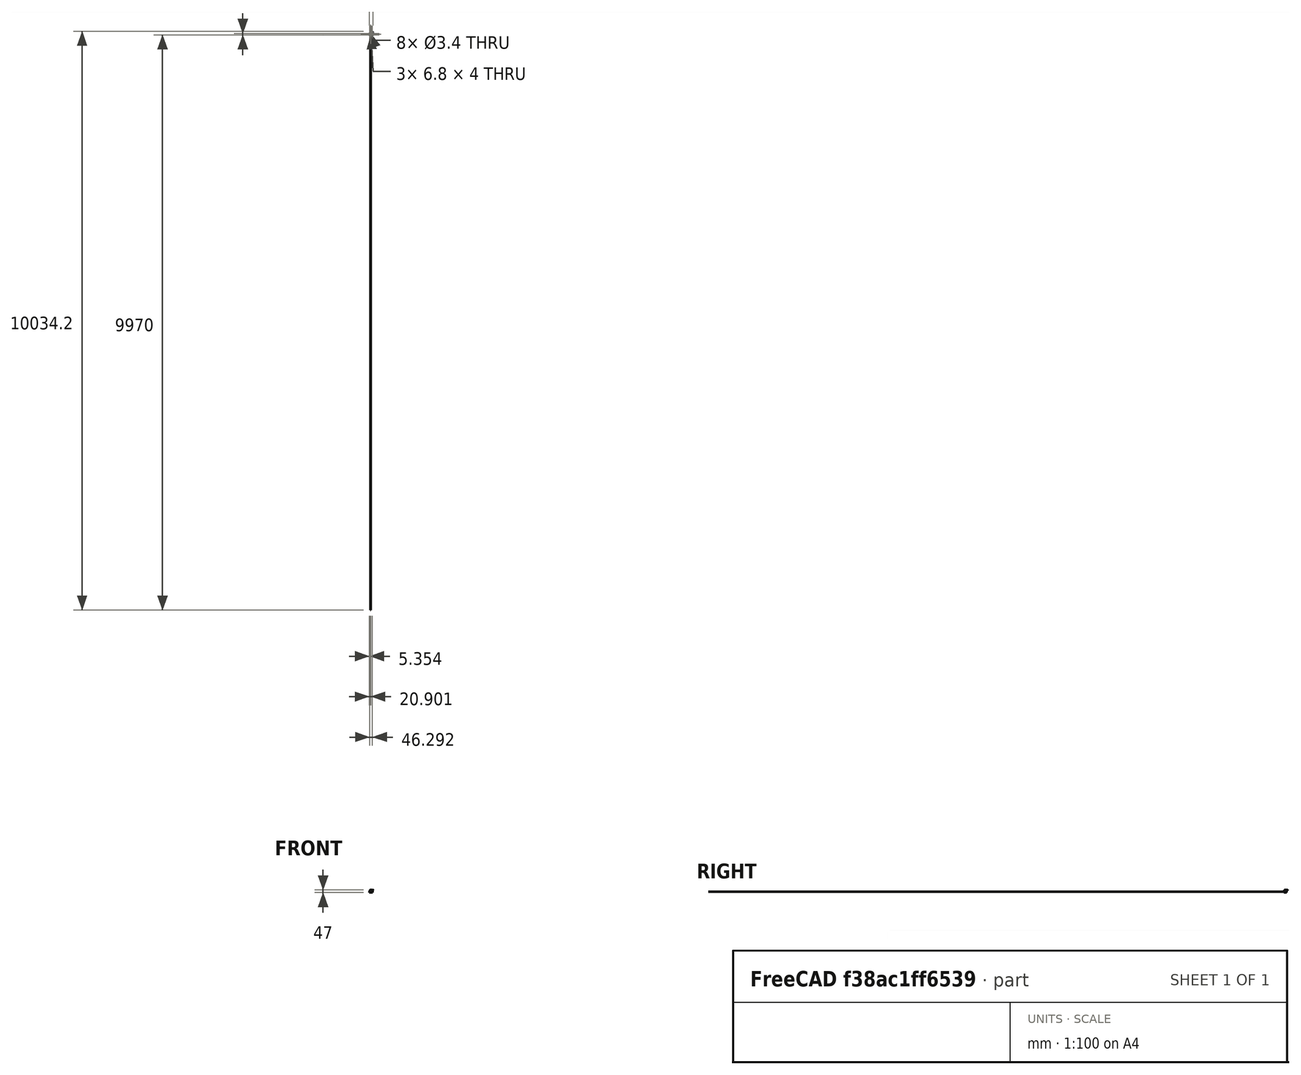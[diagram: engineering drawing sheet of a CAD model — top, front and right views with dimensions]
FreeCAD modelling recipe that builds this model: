
FCSTD DOCUMENT  (FreeCAD 0.14R2935 (Git))
Label: cabeza
License: CC-BY 3.0
LicenseURL: http://creativecommons.org/licenses/by/3.0/
objects: Sketcher::SketchObject×20, PartDesign::Pocket×14, PartDesign::Chamfer×8, PartDesign::Pad×7, PartDesign::Fillet×6, App::DocumentObjectGroup×5, Part::Box×4, Part::FeaturePython×3, Part::Feature×2, Part::Cylinder×1, Mesh::Feature×1, Part::Cut×1
note: 87 computed .brp shape members not serialized (recipe doc carries the construction recipe); baked Part::Feature solids carry a one-line shape summary decoded from their .brp

FEATURE [Part::Box] Box
  Height = 2
  Length = 10
  Width = 12
FEATURE [Sketcher::SketchObject] Sketch
  Placement = pos=(0,0,2) rot=(0,0,1;0rad)
  Support = -> Box [Face6]
  sketch-geometry (1):
    g0: Circle CenterX=4.90431 CenterY=7.27272 CenterZ=0 NormalX=0 NormalY=0 NormalZ=1 Radius=4.25
  constraints (1):
    c: Radius(g0) = 4.25
FEATURE [PartDesign::Pad] Pad
  Length = 2
  Length2 = 100
  Sketch = -> Sketch
  Type = 0
FEATURE [Sketcher::SketchObject] Sketch001
  ExternalGeometry = -> [Pad]
  Placement = pos=(0,0,4) rot=(0,0,1;0rad)
  Support = -> Pad [Face8]
  sketch-geometry (1):
    g0: Circle CenterX=4.90431 CenterY=7.27272 CenterZ=0 NormalX=0 NormalY=0 NormalZ=1 Radius=2
  constraints (2):
    c: Coincident(g0,g-3)
    c: Radius(g0) = 2
FEATURE [PartDesign::Pocket] Pocket  label="camara"
  Length = 1
  Sketch = -> Sketch001
  Type = 0
FEATURE [App::DocumentObjectGroup] Grupo  label="Camera"
  Group = -> [Box,Pad,Pocket]
FEATURE [Part::FeaturePython] Clone  label="camara001"  # Draft clone (typed FeaturePython)
  Objects = -> [Pocket]
  Placement = pos=(1.5,0,-16) rot=(0,0,1;0rad)
  Scale = (1,1,1)
FEATURE [Part::Cylinder] Cylinder
  Angle = 360
  Height = 2
  Radius = 11.5
FEATURE [Sketcher::SketchObject] Sketch002
  Placement = pos=(0,0,2) rot=(0,0,1;0rad)
  Support = -> Cylinder [Face2]
  sketch-geometry (6):
    g0: LineSegment StartX=-3 StartY=3 StartZ=0 EndX=3 EndY=3 EndZ=0
    g1: LineSegment StartX=3 StartY=3 StartZ=0 EndX=3 EndY=-3 EndZ=0
    g2: LineSegment StartX=3 StartY=-3 StartZ=0 EndX=-3 EndY=-3 EndZ=0
    g3: LineSegment StartX=-3 StartY=-3 StartZ=0 EndX=-3 EndY=3 EndZ=0
    g4: LineSegment [constr] StartX=-3 StartY=3 StartZ=0 EndX=3 EndY=-3 EndZ=0
    g5: LineSegment [constr] StartX=3 StartY=3 StartZ=0 EndX=-3 EndY=-3 EndZ=0
  constraints (16):
    c: Coincident(g0,g1)
    c: Coincident(g1,g2)
    c: Coincident(g2,g3)
    c: Coincident(g3,g0)
    c: Horizontal(g0)
    c: Horizontal(g2)
    c: Vertical(g1)
    c: Vertical(g3)
    c: Equal(g0,g1)
    c: DistanceX(g2) = -6
    c: Coincident(g5,g0)
    c: Coincident(g5,g2)
    c: Coincident(g4,g1)
    c: Coincident(g4,g0)
    c: PointOnObject(g-1,g5)
    c: PointOnObject(g-1,g4)
FEATURE [PartDesign::Pad] Pad001
  Length = 1
  Length2 = 100
  Sketch = -> Sketch002
  Type = 0
FEATURE [Sketcher::SketchObject] Sketch003
  Placement = pos=(0,0,3) rot=(0,0,1;0rad)
  Support = -> Pad001 [Face8]
  sketch-geometry (1):
    g0: Circle CenterX=0 CenterY=0 CenterZ=0 NormalX=0 NormalY=0 NormalZ=1 Radius=2
  constraints (2):
    c: Coincident(g0,g-1)
    c: Radius(g0) = 2
FEATURE [PartDesign::Pocket] Pocket001
  Length = 1
  Sketch = -> Sketch003
  Type = 0
FEATURE [Sketcher::SketchObject] Sketch004
  ExternalGeometry = -> [Pocket001]
  Placement = pos=(0,0,2) rot=(0,0,1;0rad)
  Support = -> Pocket001 [Face2]
  sketch-geometry (28):
    g0: LineSegment StartX=-3 StartY=9.7 StartZ=0 EndX=3 EndY=9.7 EndZ=0
    g1: LineSegment StartX=3 StartY=9.7 StartZ=0 EndX=3 EndY=3.7 EndZ=0
    g2: LineSegment StartX=3 StartY=3.7 StartZ=0 EndX=-3 EndY=3.7 EndZ=0
    g3: LineSegment StartX=-3 StartY=3.7 StartZ=0 EndX=-3 EndY=9.7 EndZ=0
    g4: LineSegment StartX=-9.7 StartY=3 StartZ=0 EndX=-3.7 EndY=3 EndZ=0
    g5: LineSegment StartX=-3.7 StartY=3 StartZ=0 EndX=-3.7 EndY=-3 EndZ=0
    g6: LineSegment StartX=-3.7 StartY=-3 StartZ=0 EndX=-9.7 EndY=-3 EndZ=0
    g7: LineSegment StartX=-9.7 StartY=-3 StartZ=0 EndX=-9.7 EndY=3 EndZ=0
    g8: LineSegment StartX=-3 StartY=-3.7 StartZ=0 EndX=3 EndY=-3.7 EndZ=0
    g9: LineSegment StartX=3 StartY=-3.7 StartZ=0 EndX=3 EndY=-9.7 EndZ=0
    g10: LineSegment StartX=3 StartY=-9.7 StartZ=0 EndX=-3 EndY=-9.7 EndZ=0
    g11: LineSegment StartX=-3 StartY=-9.7 StartZ=0 EndX=-3 EndY=-3.7 EndZ=0
    g12: LineSegment StartX=3.7 StartY=3 StartZ=0 EndX=9.7 EndY=3 EndZ=0
    g13: LineSegment StartX=9.7 StartY=3 StartZ=0 EndX=9.7 EndY=-3 EndZ=0
    g14: LineSegment StartX=9.7 StartY=-3 StartZ=0 EndX=3.7 EndY=-3 EndZ=0
    g15: LineSegment StartX=3.7 StartY=-3 StartZ=0 EndX=3.7 EndY=3 EndZ=0
    g16: LineSegment [constr] StartX=-3 StartY=9.7 StartZ=0 EndX=3 EndY=3.7 EndZ=0
    g17: LineSegment [constr] StartX=3 StartY=9.7 StartZ=0 EndX=-3 EndY=3.7 EndZ=0
    g18: LineSegment [constr] StartX=3.7 StartY=3 StartZ=0 EndX=9.7 EndY=-3 EndZ=0
    g19: LineSegment [constr] StartX=9.7 StartY=3 StartZ=0 EndX=3.7 EndY=-3 EndZ=0
    g20: LineSegment [constr] StartX=-9.7 StartY=3 StartZ=0 EndX=-3.7 EndY=-3 EndZ=0
    g21: LineSegment [constr] StartX=-3.7 StartY=3 StartZ=0 EndX=-9.7 EndY=-3 EndZ=0
    g22: LineSegment [constr] StartX=-3 StartY=-3.7 StartZ=0 EndX=3 EndY=-9.7 EndZ=0
    g23: LineSegment [constr] StartX=3 StartY=-3.7 StartZ=0 EndX=-3 EndY=-9.7 EndZ=0
    g24: GeomPoint [constr] X=0 Y=-6.7 Z=0
    g25: GeomPoint [constr] X=6.7 Y=0 Z=0
    g26: GeomPoint [constr] X=-6.7 Y=0 Z=0
    g27: GeomPoint [constr] X=0 Y=6.7 Z=0
  constraints (72):
    c: Coincident(g0,g1)
    c: Coincident(g1,g2)
    c: Coincident(g2,g3)
    c: Coincident(g3,g0)
    c: Horizontal(g0)
    c: Horizontal(g2)
    c: Vertical(g1)
    c: Vertical(g3)
    c: Equal(g3,g2)
    c: Equal(g2,g-3)
    c: Coincident(g4,g5)
    c: Coincident(g5,g6)
    c: Coincident(g6,g7)
    c: Coincident(g7,g4)
    c: Horizontal(g4)
    c: Horizontal(g6)
    c: Vertical(g5)
    c: Vertical(g7)
    c: Coincident(g8,g9)
    c: Coincident(g9,g10)
    c: Coincident(g10,g11)
    c: Coincident(g11,g8)
    c: Horizontal(g8)
    c: Horizontal(g10)
    c: Vertical(g9)
    c: Vertical(g11)
    c: Coincident(g12,g13)
    c: Coincident(g13,g14)
    c: Coincident(g14,g15)
    c: Coincident(g15,g12)
    c: Horizontal(g12)
    c: Horizontal(g14)
    c: Vertical(g13)
    c: Vertical(g15)
    c: Equal(g12,g15)
    c: Equal(g15,g8)
    c: Equal(g8,g9)
    c: Equal(g9,g6)
    c: Equal(g6,g5)
    c: Equal(g2,g12)
    c: Coincident(g23,g10)
    c: Coincident(g22,g8)
    c: Coincident(g23,g8)
    c: Coincident(g22,g9)
    c: PointOnObject(g24,g-2)
    c: PointOnObject(g24,g23)
    c: PointOnObject(g24,g22)
    c: Coincident(g19,g12)
    c: Coincident(g18,g13)
    c: Coincident(g18,g12)
    c: Coincident(g19,g14)
    c: Coincident(g16,g1)
    c: Coincident(g17,g0)
    c: Coincident(g17,g2)
    c: Coincident(g16,g0)
    c: Coincident(g21,g4)
    c: Coincident(g20,g4)
    c: Coincident(g21,g6)
    c: Coincident(g20,g5)
    c: PointOnObject(g25,g-1)
    c: PointOnObject(g26,g-1)
    c: PointOnObject(g27,g-2)
    c: PointOnObject(g26,g20)
    c: PointOnObject(g26,g21)
    c: PointOnObject(g25,g19)
    c: PointOnObject(g25,g18)
    c: PointOnObject(g27,g16)
    c: PointOnObject(g27,g17)
    c: Distance(g-4,g4) = 0.7
    c: Distance(g-4,g8) = 0.7
    c: Distance(g-5,g14) = 0.7
    c: Distance(g2,g-4) = 0.7
FEATURE [PartDesign::Pad] Pad002
  Length = 1
  Length2 = 100
  Sketch = -> Sketch004
  Type = 0
FEATURE [Sketcher::SketchObject] Sketch005
  ExternalGeometry = -> [Pad002]
  Placement = pos=(0,0,3) rot=(0,0,1;0rad)
  Support = -> Pad002 [Face26]
  sketch-geometry (4):
    g0: Circle CenterX=0 CenterY=6.61559 CenterZ=0 NormalX=0 NormalY=0 NormalZ=1 Radius=2
    g1: Circle CenterX=-6.61558 CenterY=0 CenterZ=0 NormalX=0 NormalY=0 NormalZ=1 Radius=2
    g2: Circle CenterX=6.71215 CenterY=0 CenterZ=0 NormalX=0 NormalY=0 NormalZ=1 Radius=2
    g3: Circle CenterX=0 CenterY=-6.71214 CenterZ=0 NormalX=0 NormalY=0 NormalZ=1 Radius=2
  constraints (8):
    c: Equal(g1,g0)
    c: Equal(g0,g-3)
    c: Equal(g-3,g2)
    c: Equal(g2,g3)
    c: PointOnObject(g2,g-1)
    c: PointOnObject(g0,g-2)
    c: PointOnObject(g1,g-1)
    c: PointOnObject(g3,g-2)
FEATURE [PartDesign::Pocket] Pocket002
  Length = 1
  Sketch = -> Sketch005
  Type = 0
FEATURE [Part::FeaturePython] Clone001  label="ojo001"  # Draft clone (typed FeaturePython)
  Objects = -> [Pocket002]
  Placement = pos=(-7,-6,-13) rot=(0,0,1;0rad)
  Scale = (1,1,1)
FEATURE [App::DocumentObjectGroup] Grupo001  label="ojo"
  Group = -> [Cylinder,Pad001,Pocket001,Pad002,Pocket002]
FEATURE [Part::FeaturePython] Clone002  label="ojo002"  # Draft clone (typed FeaturePython)
  Objects = -> [Pocket002]
  Placement = pos=(21,-7,-13) rot=(0,0,1;0rad)
  Scale = (1,1,1)
FEATURE [Part::Box] Box001
  Height = 4
  Length = 35
  Placement = pos=(-11,-31,-17) rot=(0,0,1;0rad)
  Width = 47
FEATURE [Mesh::Feature] _g_servo  label="9g_servo"
  Placement = pos=(0,-7,-24) rot=(0.57735,0.57735,0.57735;2.0944rad)
FEATURE [Sketcher::SketchObject] Sketch006
  ExternalGeometry = -> [Box001]
  Placement = pos=(-11,-31,-17) rot=(1,0,0;3.14159rad)
  Support = -> Box001 [Face5]
  sketch-geometry (9):
    g0: LineSegment StartX=6.5 StartY=-7.91944 StartZ=0 EndX=13.302 EndY=-7.91944 EndZ=0
    g1: LineSegment StartX=13.302 StartY=-7.91944 StartZ=0 EndX=13.302 EndY=-11.9194 EndZ=0
    g2: LineSegment StartX=13.302 StartY=-11.9194 StartZ=0 EndX=6.5 EndY=-11.9194 EndZ=0
    g3: LineSegment StartX=6.5 StartY=-11.9194 StartZ=0 EndX=6.5 EndY=-7.91944 EndZ=0
    g4: LineSegment StartX=6.5 StartY=-35.9194 StartZ=0 EndX=13.302 EndY=-35.9194 EndZ=0
    g5: LineSegment StartX=13.302 StartY=-35.9194 StartZ=0 EndX=13.302 EndY=-39.9194 EndZ=0
    g6: LineSegment StartX=13.302 StartY=-39.9194 StartZ=0 EndX=6.5 EndY=-39.9194 EndZ=0
    g7: LineSegment StartX=6.5 StartY=-39.9194 StartZ=0 EndX=6.5 EndY=-35.9194 EndZ=0
    g8: LineSegment [constr] StartX=6.5 StartY=0 StartZ=0 EndX=6.5 EndY=-47 EndZ=0
  constraints (27):
    c: Coincident(g0,g1)
    c: Coincident(g1,g2)
    c: Coincident(g2,g3)
    c: Coincident(g3,g0)
    c: Horizontal(g0)
    c: Horizontal(g2)
    c: Vertical(g1)
    c: Vertical(g3)
    c: Coincident(g4,g5)
    c: Coincident(g5,g6)
    c: Coincident(g6,g7)
    c: Coincident(g7,g4)
    c: Horizontal(g4)
    c: Horizontal(g6)
    c: Vertical(g5)
    c: Vertical(g7)
    c: Equal(g2,g4)
    c: Vertical(g8)
    c: PointOnObject(g8,g-3)
    c: PointOnObject(g8,g-1)
    c: PointOnObject(g0,g8)
    c: PointOnObject(g4,g8)
    c: Equal(g1,g5)
    c: DistanceY(g1) = -4
    c: Distance(g2,g4) = 24
    c: Distance(g6,g8) = 7.08056
    c: Distance(g-3,g8) = 6.5
FEATURE [PartDesign::Pad] Pad003
  Length = 14
  Length2 = 100
  Placement = pos=(-11,-31,-17) rot=(0,0,1;0rad)
  Sketch = -> Sketch006
  Type = 0
FEATURE [Sketcher::SketchObject] Sketch007
  ExternalGeometry = -> [Pad003]
  Placement = pos=(2.30204,-31,-17) rot=(0.57735,0.57735,0.57735;2.0944rad)
  Support = -> Pad003 [Face7]
  sketch-geometry (3):
    g0: Circle CenterX=9.93523 CenterY=-7.03791 CenterZ=0 NormalX=0 NormalY=0 NormalZ=1 Radius=1.64716
    g1: Circle CenterX=37.8885 CenterY=-7.03791 CenterZ=0 NormalX=0 NormalY=0 NormalZ=1 Radius=1.53113
    g2: LineSegment [constr] StartX=35.9194 StartY=-7.03791 StartZ=0 EndX=11.9194 EndY=-7.03791 EndZ=0
  constraints (5):
    c: PointOnObject(g2,g-3)
    c: Horizontal(g2)
    c: PointOnObject(g2,g-4)
    c: PointOnObject(g0,g2)
    c: PointOnObject(g1,g2)
FEATURE [PartDesign::Pocket] Pocket003
  Length = 7
  Placement = pos=(-11,-31,-17) rot=(0,0,1;0rad)
  Sketch = -> Sketch007
  Type = 0
FEATURE [Sketcher::SketchObject] Sketch008
  ExternalGeometry = -> [Pocket003]
  Placement = pos=(-11,-31,-17) rot=(1,0,0;3.14159rad)
  Support = -> Pocket003 [Face5]
  sketch-geometry (6):
    g0: ArcOfCircle CenterX=31.6459 CenterY=-23.9498 CenterZ=0 NormalX=0 NormalY=0 NormalZ=1 Radius=11.5 StartAngle=5.00835 EndAngle=7.55802
    g1: LineSegment [constr] StartX=35 StartY=-12.9498 StartZ=0 EndX=0 EndY=-12.9498 EndZ=0
    g2: LineSegment [constr] StartX=35 StartY=-34.9498 StartZ=0 EndX=0 EndY=-34.9498 EndZ=0
    g3: ArcOfCircle CenterX=3.3541 CenterY=-23.9498 CenterZ=0 NormalX=0 NormalY=0 NormalZ=1 Radius=11.5 StartAngle=1.86676 EndAngle=4.41643
    g4: LineSegment StartX=35 StartY=-12.9498 StartZ=0 EndX=35 EndY=-34.9498 EndZ=0
    g5: LineSegment StartX=0 StartY=-12.9498 StartZ=0 EndX=0 EndY=-34.9498 EndZ=0
  constraints (20):
    c: PointOnObject(g0,g-3)
    c: PointOnObject(g0,g-3)
    c: Distance(g0,g0) = 22
    c: Radius(g0) = 11.5
    c: Horizontal(g1)
    c: Horizontal(g2)
    c: Distance(g-3,g0) = 12.9498
    c: Coincident(g1,g0)
    c: PointOnObject(g1,g-2)
    c: Coincident(g2,g0)
    c: PointOnObject(g2,g-2)
    c: Coincident(g3,g2)
    c: Coincident(g3,g1)
    c: Equal(g0,g3)
    c: Vertical(g4)
    c: Coincident(g4,g0)
    c: Coincident(g4,g0)
    c: Vertical(g5)
    c: Coincident(g5,g1)
    c: Coincident(g5,g2)
FEATURE [PartDesign::Pad] Pad004
  Length = 4
  Length2 = 100
  Placement = pos=(-11,-31,-17) rot=(0,0,1;0rad)
  Reversed = true
  Sketch = -> Sketch008
  Type = 0
FEATURE [Sketcher::SketchObject] Sketch009
  ExternalGeometry = -> [Pad004]
  Placement = pos=(-11,-31,-13) rot=(0,0,1;0rad)
  Support = -> Pad004 [Face4]
  sketch-geometry (6):
    g0: Circle CenterX=17.5 CenterY=38.5843 CenterZ=0 NormalX=0 NormalY=0 NormalZ=1 Radius=4.5
    g1: LineSegment [constr] StartX=0 StartY=38.5843 StartZ=0 EndX=17.5 EndY=38.5843 EndZ=0
    g2: LineSegment [constr] StartX=17.5 StartY=38.5843 StartZ=0 EndX=35 EndY=38.5843 EndZ=0
    g3: Circle CenterX=-5.6459 CenterY=23.9498 CenterZ=0 NormalX=0 NormalY=0 NormalZ=1 Radius=1.7
    g4: Circle CenterX=40.6459 CenterY=23.9498 CenterZ=0 NormalX=0 NormalY=0 NormalZ=1 Radius=1.7
    g5: LineSegment [constr] StartX=-8.1459 StartY=23.9498 StartZ=0 EndX=43.1459 EndY=23.9498 EndZ=0
  constraints (19):
    c: Horizontal(g1)
    c: Horizontal(g2)
    c: PointOnObject(g1,g-2)
    c: PointOnObject(g2,g-3)
    c: Coincident(g2,g0)
    c: Coincident(g1,g0)
    c: Equal(g1,g2)
    c: Radius(g0) = 4.5
    c: DistanceY(g-1,g2) = 38.5843
    c: Horizontal(g5)
    c: PointOnObject(g5,g-5)
    c: PointOnObject(g5,g-4)
    c: PointOnObject(g3,g5)
    c: PointOnObject(g4,g5)
    c: Radius(g4) = 1.7
    c: Radius(g3) = 1.7
    c: Distance(g3,g5) = 2.5
    c: Distance(g4,g5) = 2.5
    c: PointOnObject(g-5,g5)
FEATURE [PartDesign::Pocket] Pocket004
  Length = 4
  Placement = pos=(-11,-31,-17) rot=(0,0,1;0rad)
  Sketch = -> Sketch009
  Type = 0
FEATURE [Part::Feature] Pocket004001  label="Pocket005"
  shape: bbox 51.29 x 47 x 18 mm, 26 faces (baked)
FEATURE [PartDesign::Chamfer] Chamfer
  Base = -> Pocket004001 [Edge6]
  Size = 10
FEATURE [PartDesign::Chamfer] Chamfer001
  Base = -> Chamfer [Edge3]
  Size = 10
FEATURE [PartDesign::Fillet] Fillet
  Base = -> Chamfer001 [Edge3]
  Radius = 10
FEATURE [PartDesign::Fillet] Fillet001
  Base = -> Fillet [Edge3]
  Radius = 10
FEATURE [PartDesign::Fillet] Fillet002
  Base = -> Fillet001 [Edge45]
  Radius = 3
FEATURE [PartDesign::Fillet] Fillet003
  Base = -> Fillet002 [Edge43]
  Radius = 3
FEATURE [PartDesign::Chamfer] Chamfer002
  Base = -> Fillet003 [Edge46]
  Size = 10
FEATURE [PartDesign::Chamfer] Chamfer003
  Base = -> Chamfer002 [Edge29]
  Size = 10
FEATURE [Sketcher::SketchObject] Sketch010
  ExternalGeometry = -> [Chamfer003]
  Placement = pos=(0,0,-13) rot=(0,0,1;0rad)
  Support = -> Chamfer003 [Face29]
  sketch-geometry (9):
    g0: LineSegment [constr] StartX=-16.6459 StartY=-7.0502 StartZ=0 EndX=29.6459 EndY=-7.0502 EndZ=0
    g1: Circle CenterX=3.3541 CenterY=-7.0502 CenterZ=0 NormalX=0 NormalY=0 NormalZ=1 Radius=1.7
    g2: Circle CenterX=9.6459 CenterY=-7.0502 CenterZ=0 NormalX=0 NormalY=0 NormalZ=1 Radius=1.7
    g3: LineSegment [constr] StartX=-1 StartY=-7.0502 StartZ=0 EndX=-1 EndY=-31 EndZ=0
    g4: LineSegment [constr] StartX=14 StartY=-7.0502 StartZ=0 EndX=14 EndY=-31 EndZ=0
    g5: LineSegment StartX=-1 StartY=-23.5 StartZ=0 EndX=14 EndY=-23.5 EndZ=0
    g6: LineSegment StartX=14 StartY=-23.5 StartZ=0 EndX=14 EndY=-26.5 EndZ=0
    g7: LineSegment StartX=14 StartY=-26.5 StartZ=0 EndX=-1 EndY=-26.5 EndZ=0
    g8: LineSegment StartX=-1 StartY=-26.5 StartZ=0 EndX=-1 EndY=-23.5 EndZ=0
  constraints (27):
    c: Horizontal(g0)
    c: Coincident(g0,g-4)
    c: Coincident(g0,g-3)
    c: PointOnObject(g1,g0)
    c: PointOnObject(g2,g0)
    c: Radius(g2) = 1.7
    c: Radius(g1) = 1.7
    c: Distance(g0,g1) = 20
    c: Distance(g2,g0) = 20
    c: Vertical(g3)
    c: Coincident(g3,g-5)
    c: PointOnObject(g3,g0)
    c: Vertical(g4)
    c: Coincident(g4,g-5)
    c: PointOnObject(g4,g0)
    c: Coincident(g5,g6)
    c: Coincident(g6,g7)
    c: Coincident(g7,g8)
    c: Coincident(g8,g5)
    c: Horizontal(g5)
    c: Horizontal(g7)
    c: Vertical(g6)
    c: Vertical(g8)
    c: DistanceY(g6) = -3
    c: PointOnObject(g7,g3)
    c: PointOnObject(g6,g4)
    c: Distance(g7,g3) = 4.5
FEATURE [PartDesign::Pocket] Pocket004002
  Length = 5
  Sketch = -> Sketch010
  Type = 0
FEATURE [Sketcher::SketchObject] Sketch011
  Placement = pos=(0,8.91944,0) rot=(0,0.707107,0.707107;3.14159rad)
  Support = -> Pocket004002 [Face18]
  sketch-geometry (4):
    g0: LineSegment StartX=-1.74892 StartY=-26.7435 StartZ=0 EndX=3.95108 EndY=-26.7435 EndZ=0
    g1: LineSegment StartX=3.95108 StartY=-26.7435 StartZ=0 EndX=3.95108 EndY=-29.3435 EndZ=0
    g2: LineSegment StartX=3.95108 StartY=-29.3435 StartZ=0 EndX=-1.74892 EndY=-29.3435 EndZ=0
    g3: LineSegment StartX=-1.74892 StartY=-29.3435 StartZ=0 EndX=-1.74892 EndY=-26.7435 EndZ=0
  constraints (10):
    c: Coincident(g0,g1)
    c: Coincident(g1,g2)
    c: Coincident(g2,g3)
    c: Coincident(g3,g0)
    c: Horizontal(g0)
    c: Horizontal(g2)
    c: Vertical(g1)
    c: Vertical(g3)
    c: DistanceY(g1) = -2.6
    c: DistanceX(g2) = -5.7
FEATURE [PartDesign::Pocket] Pocket004003
  Length = 5
  Sketch = -> Sketch011
  Type = 1
FEATURE [Sketcher::SketchObject] Sketch012
  ExternalGeometry = -> [Pocket004003]
  Placement = pos=(0,0,-31) rot=(1,0,0;3.14159rad)
  Support = -> Pocket004003 [Face37]
  sketch-geometry (6):
    g0: LineSegment [constr] StartX=-4.5 StartY=23.0806 StartZ=0 EndX=2.30204 EndY=19.0806 EndZ=0
    g1: LineSegment [constr] StartX=2.30204 StartY=23.0806 StartZ=0 EndX=-4.5 EndY=19.0806 EndZ=0
    g2: Circle CenterX=-1.09898 CenterY=21.0806 CenterZ=0 NormalX=0 NormalY=0 NormalZ=1 Radius=1.7
    g3: LineSegment [constr] StartX=-4.5 StartY=-4.91944 StartZ=0 EndX=2.30204 EndY=-8.91944 EndZ=0
    g4: LineSegment [constr] StartX=2.30204 StartY=-4.91944 StartZ=0 EndX=-4.5 EndY=-8.91944 EndZ=0
    g5: Circle CenterX=-1.09898 CenterY=-6.91944 CenterZ=0 NormalX=0 NormalY=0 NormalZ=1 Radius=1.7
  constraints (14):
    c: Coincident(g1,g-4)
    c: Coincident(g1,g-3)
    c: Coincident(g0,g-4)
    c: Coincident(g0,g-3)
    c: PointOnObject(g2,g1)
    c: PointOnObject(g2,g0)
    c: Radius(g2) = 1.7
    c: Coincident(g4,g-6)
    c: Coincident(g4,g-5)
    c: Coincident(g3,g-6)
    c: Coincident(g3,g-5)
    c: PointOnObject(g5,g4)
    c: PointOnObject(g5,g3)
    c: Radius(g5) = 1.7
FEATURE [PartDesign::Pocket] Pocket004004
  Length = 4
  Sketch = -> Sketch012
  Type = 0
FEATURE [Part::Box] Box002
  Height = 26
  Length = 36
  Placement = pos=(-12,-31,-43) rot=(0,0,1;0rad)
  Width = 47
FEATURE [PartDesign::Pocket] Pocket004005
  Length = 4
  Sketch = -> Sketch012
  Type = 0
FEATURE [Part::Feature] Pocket004006  label="cara"
  shape: bbox 51.29 x 47 x 18 mm, 50 faces (baked)
FEATURE [PartDesign::Fillet] Fillet004
  Base = -> Box002 [Edge7]
  Placement = pos=(-12,-31,-43) rot=(0,0,1;0rad)
  Radius = 17
FEATURE [PartDesign::Fillet] Fillet005
  Base = -> Fillet004 [Edge15]
  Placement = pos=(-12,-31,-43) rot=(0,0,1;0rad)
  Radius = 17
FEATURE [PartDesign::Chamfer] Chamfer004
  Base = -> Fillet005 [Edge16]
  Placement = pos=(-12,-31,-43) rot=(0,0,1;0rad)
  Size = 10
FEATURE [PartDesign::Chamfer] Chamfer005
  Base = -> Chamfer004 [Edge16]
  Placement = pos=(-12,-31,-43) rot=(0,0,1;0rad)
  Size = 10
FEATURE [Part::Box] Box003
  Height = 26
  Length = 36
  Placement = pos=(-12,-31,-43) rot=(0,0,1;0rad)
  Width = 10
FEATURE [Part::Cut] Cut
  Base = -> Chamfer005
  Tool = -> Box003
FEATURE [Sketcher::SketchObject] Sketch013
  ExternalGeometry = -> [Cut]
  Placement = pos=(0,-21,0) rot=(1,0,0;1.5708rad)
  Support = -> Cut [Face7]
  sketch-geometry (4):
    g0: LineSegment StartX=-9 StartY=-17 StartZ=0 EndX=21 EndY=-17 EndZ=0
    g1: LineSegment StartX=21 StartY=-17 StartZ=0 EndX=21 EndY=-40 EndZ=0
    g2: LineSegment StartX=21 StartY=-40 StartZ=0 EndX=-9 EndY=-40 EndZ=0
    g3: LineSegment StartX=-9 StartY=-40 StartZ=0 EndX=-9 EndY=-17 EndZ=0
  constraints (12):
    c: Coincident(g0,g1)
    c: Coincident(g1,g2)
    c: Coincident(g2,g3)
    c: Coincident(g3,g0)
    c: Horizontal(g0)
    c: Horizontal(g2)
    c: Vertical(g1)
    c: Vertical(g3)
    c: PointOnObject(g0,g-5)
    c: Distance(g-5,g0) = 3
    c: Distance(g-5,g0) = 3
    c: Distance(g2,g-6) = 3
FEATURE [PartDesign::Pocket] Pocket004007
  Length = 27
  Sketch = -> Sketch013
  Type = 0
FEATURE [Sketcher::SketchObject] Sketch014
  ExternalGeometry = -> [Pocket004007]
  Placement = pos=(0,0,-17) rot=(0,0,1;0rad)
  Support = -> Pocket004007 [Face1]
  sketch-geometry (4):
    g0: LineSegment StartX=-0.588067 StartY=13.0845 StartZ=0 EndX=12.9735 EndY=13.0845 EndZ=0
    g1: LineSegment StartX=12.9735 StartY=13.0845 StartZ=0 EndX=12.9735 EndY=6 EndZ=0
    g2: LineSegment StartX=12.9735 StartY=6 StartZ=0 EndX=-0.588067 EndY=6 EndZ=0
    g3: LineSegment StartX=-0.588067 StartY=6 StartZ=0 EndX=-0.588067 EndY=13.0845 EndZ=0
  constraints (9):
    c: Coincident(g0,g1)
    c: Coincident(g1,g2)
    c: Coincident(g2,g3)
    c: Coincident(g3,g0)
    c: Horizontal(g0)
    c: Horizontal(g2)
    c: Vertical(g1)
    c: Vertical(g3)
    c: PointOnObject(g2,g-3)
FEATURE [PartDesign::Pocket] Pocket004008
  Length = 23
  Sketch = -> Sketch014
  Type = 0
FEATURE [Sketcher::SketchObject] Sketch015
  ExternalGeometry = -> [Pocket004008]
  Placement = pos=(0,0,-43) rot=(1,0,0;3.14159rad)
  Support = -> Pocket004008 [Face15]
  sketch-geometry (8):
    g0: LineSegment StartX=-22 StartY=21 StartZ=0 EndX=-12 EndY=21 EndZ=0
    g1: LineSegment StartX=-12 StartY=21 StartZ=0 EndX=-12 EndY=1 EndZ=0
    g2: LineSegment StartX=-12 StartY=1 StartZ=0 EndX=-22 EndY=1 EndZ=0
    g3: LineSegment StartX=-22 StartY=1 StartZ=0 EndX=-22 EndY=21 EndZ=0
    g4: LineSegment StartX=34 StartY=21 StartZ=0 EndX=24 EndY=21 EndZ=0
    g5: LineSegment StartX=24 StartY=21 StartZ=0 EndX=24 EndY=1 EndZ=0
    g6: LineSegment StartX=24 StartY=1 StartZ=0 EndX=34 EndY=1 EndZ=0
    g7: LineSegment StartX=34 StartY=1 StartZ=0 EndX=34 EndY=21 EndZ=0
  constraints (22):
    c: Coincident(g0,g1)
    c: Coincident(g1,g2)
    c: Coincident(g2,g3)
    c: Coincident(g3,g0)
    c: Horizontal(g0)
    c: Horizontal(g2)
    c: Vertical(g1)
    c: Vertical(g3)
    c: Coincident(g-3,g0)
    c: Coincident(g1,g-3)
    c: Coincident(g4,g5)
    c: Coincident(g5,g6)
    c: Coincident(g6,g7)
    c: Coincident(g7,g4)
    c: Horizontal(g4)
    c: Horizontal(g6)
    c: Vertical(g5)
    c: Vertical(g7)
    c: Coincident(g5,g-4)
    c: Coincident(g4,g-4)
    c: Equal(g0,g4)
    c: DistanceX(g2) = -10
FEATURE [PartDesign::Pad] Pad005
  Length = 25
  Length2 = 100
  Reversed = true
  Sketch = -> Sketch015
  Type = 0
FEATURE [PartDesign::Chamfer] Chamfer006
  Base = -> Pad005 [Edge48]
  Size = 9
FEATURE [PartDesign::Chamfer] Chamfer007
  Base = -> Chamfer006 [Edge67]
  Size = 9
FEATURE [Sketcher::SketchObject] Sketch016
  ExternalGeometry = -> [Chamfer007]
  Placement = pos=(2.5,0,-2.5) rot=(0.357407,-0.357407,-0.862856;1.71777rad)
  Support = -> Chamfer007 [Face21]
  sketch-geometry (4):
    g0: LineSegment StartX=4 StartY=-28.1482 StartZ=0 EndX=19 EndY=-28.1482 EndZ=0
    g1: LineSegment StartX=19 StartY=-28.1482 StartZ=0 EndX=19 EndY=-31.1482 EndZ=0
    g2: LineSegment StartX=19 StartY=-31.1482 StartZ=0 EndX=4 EndY=-31.1482 EndZ=0
    g3: LineSegment StartX=4 StartY=-31.1482 StartZ=0 EndX=4 EndY=-28.1482 EndZ=0
  constraints (12):
    c: Coincident(g0,g1)
    c: Coincident(g1,g2)
    c: Coincident(g2,g3)
    c: Coincident(g3,g0)
    c: Horizontal(g0)
    c: Horizontal(g2)
    c: Vertical(g1)
    c: Vertical(g3)
    c: Distance(g2,g-3) = 3.5
    c: DistanceX(g2) = -15
    c: Distance(g1,g-4) = 2
    c: DistanceY(g1) = -3
FEATURE [PartDesign::Pocket] Pocket004009
  Length = 10
  Sketch = -> Sketch016
  Type = 0
FEATURE [Sketcher::SketchObject] Sketch017
  ExternalGeometry = -> [Pocket004009]
  Placement = pos=(3.5,0,3.5) rot=(0.357407,0.357407,0.862856;1.71777rad)
  Support = -> Pocket004009 [Face3]
  sketch-geometry (4):
    g0: LineSegment StartX=-18 StartY=-37.1335 StartZ=0 EndX=-3 EndY=-37.1335 EndZ=0
    g1: LineSegment StartX=-3 StartY=-37.1335 StartZ=0 EndX=-3 EndY=-40.1335 EndZ=0
    g2: LineSegment StartX=-3 StartY=-40.1335 StartZ=0 EndX=-18 EndY=-40.1335 EndZ=0
    g3: LineSegment StartX=-18 StartY=-40.1335 StartZ=0 EndX=-18 EndY=-37.1335 EndZ=0
  constraints (12):
    c: Coincident(g0,g1)
    c: Coincident(g1,g2)
    c: Coincident(g2,g3)
    c: Coincident(g3,g0)
    c: Horizontal(g0)
    c: Horizontal(g2)
    c: Vertical(g1)
    c: Vertical(g3)
    c: DistanceX(g2) = -15
    c: Distance(g0,g-3) = 3
    c: Distance(g2,g-4) = 3
    c: DistanceY(g1) = -3
FEATURE [PartDesign::Pocket] Pocket004010
  Length = 15
  Sketch = -> Sketch017
  Type = 0
FEATURE [Sketcher::SketchObject] Sketch018
  ExternalGeometry = -> [Pocket004010]
  Placement = pos=(0,16,0) rot=(0,0.707107,0.707107;3.14159rad)
  Support = -> Pocket004010 [Face24]
  sketch-geometry (4):
    g0: LineSegment StartX=-7 StartY=-17 StartZ=0 EndX=-5 EndY=-17 EndZ=0
    g1: LineSegment StartX=-5 StartY=-17 StartZ=0 EndX=-5 EndY=-43 EndZ=0
    g2: LineSegment StartX=-5 StartY=-43 StartZ=0 EndX=-7 EndY=-43 EndZ=0
    g3: LineSegment StartX=-7 StartY=-43 StartZ=0 EndX=-7 EndY=-17 EndZ=0
  constraints (11):
    c: Coincident(g0,g1)
    c: Coincident(g1,g2)
    c: Coincident(g2,g3)
    c: Coincident(g3,g0)
    c: Horizontal(g0)
    c: Horizontal(g2)
    c: Vertical(g1)
    c: Vertical(g3)
    c: Coincident(g1,g-4)
    c: Coincident(g0,g-4)
    c: Coincident(g0,g-3)
FEATURE [PartDesign::Pad] Pad006
  Length = 10
  Length2 = 100
  Sketch = -> Sketch018
  Type = 0
FEATURE [Sketcher::SketchObject] Sketch019
  ExternalGeometry = -> [Pad006]
  Placement = pos=(7,0,0) rot=(0.57735,0.57735,0.57735;2.0944rad)
  Support = -> Pad006 [Face35]
  sketch-geometry (3):
    g0: LineSegment StartX=16 StartY=-17 StartZ=0 EndX=26 EndY=-43 EndZ=0
    g1: LineSegment StartX=26 StartY=-43 StartZ=0 EndX=26 EndY=-17 EndZ=0
    g2: LineSegment StartX=26 StartY=-17 StartZ=0 EndX=16 EndY=-17 EndZ=0
  constraints (6):
    c: Coincident(g0,g1)
    c: Coincident(g1,g2)
    c: Coincident(g2,g0)
    c: Coincident(g1,g-4)
    c: Coincident(g0,g-3)
    c: Coincident(g0,g-4)
FEATURE [PartDesign::Pocket] Pocket004011  label="cabeza"
  Length = 5
  Sketch = -> Sketch019
  Type = 0
FEATURE [App::DocumentObjectGroup] Grupo002  label="craneo"
  Group = -> [Fillet004,Fillet005,Chamfer004,Cut,Pocket004007,Pocket004008,Pad005,Chamfer006,Chamfer007,Pocket004009,Pocket004010,Pad006,Pocket004011,Box002]
FEATURE [App::DocumentObjectGroup] Grupo003  label="Rostro"
  Group = -> [Pad003,Pocket003,Pad004,Pocket004,Pocket004001,Chamfer,Chamfer001,Fillet,Fillet001,Fillet002,Fillet003,Chamfer002,Chamfer003,Pocket004002,Pocket004003,Pocket004004,Pocket004005,Pocket004006,Box001]
FEATURE [App::DocumentObjectGroup] Grupo004  label="Montaje"
  Group = -> [Grupo,Clone,Clone001,Grupo001,Clone002,_g_servo]
